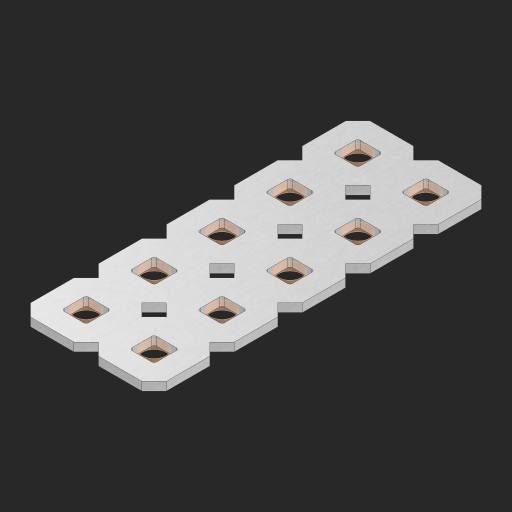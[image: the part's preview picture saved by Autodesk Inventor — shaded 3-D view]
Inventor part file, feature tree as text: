
AUTODESK INVENTOR PART (.ipt)
format: ipt  version: 2023 (Build 270158000, 158)  size: 403,968 bytes
history: native  units: in
note: dims shown in document units (in); Inventor stores cm internally (conversion verified against a paired STEP export)
features: other x11, extrude x9, sketch x2, pattern_linear x1
ambient origin geometry x8: Origin, YZ Plane, XZ Plane, XY Plane, X Axis, Y Axis, Z Axis, Center Point
bodies: Solid1 (feature_tree), Body (feature_tree)
feature tree (23):
  pattern_linear  "Rectangular Pattern1"  Spacing1=0.09in  [1 undecoded]
  sketch  "Sketch1"  dims[d1=0.5in]
  sketch  "Sketch2"  dims[d2=0.182in d3=0.09in d4=0.09in d5=0.09in d6=0.09in d7=0.09in d8=0.09in d9=0.09in d10=0.09in d11=0.02in d13=0.0in d14=0.172in d15=0.0625in d16=0.0in d19=0.5in d22=0.5in]
  other  "Srf1"
  other  "Srf126"
  other  "Srf127"
  other  "Srf128"
  other  "Srf129"
  other  "Srf268"
  other  "Srf269"
  other  "Srf270"
  other  "Srf271"
  other  "Srf272"
  other  "Circle"
  extrude  "ExtrusionSrf126"  Depth=0.09in
  extrude  "ExtrusionSrf127"  Depth=0.09in
  extrude  "ExtrusionSrf128"  Depth=0.09in
  extrude  "ExtrusionSrf129"  Depth=0.09in
  extrude  "ExtrusionSrf268"  Depth=0.09in
  extrude  "ExtrusionSrf269"  Depth=0.09in
  extrude  "ExtrusionSrf270"  Depth=0.09in
  extrude  "ExtrusionSrf271"  Depth=0.02in
  extrude  "ExtrusionSrf272"  TaperAngle=0.0deg  [1 undecoded]
note: 2 required parameter values undecoded (feature->parameter linkage not recoverable at this tier; creation-order binding heuristic only, values carry confidence <= 0.55)
